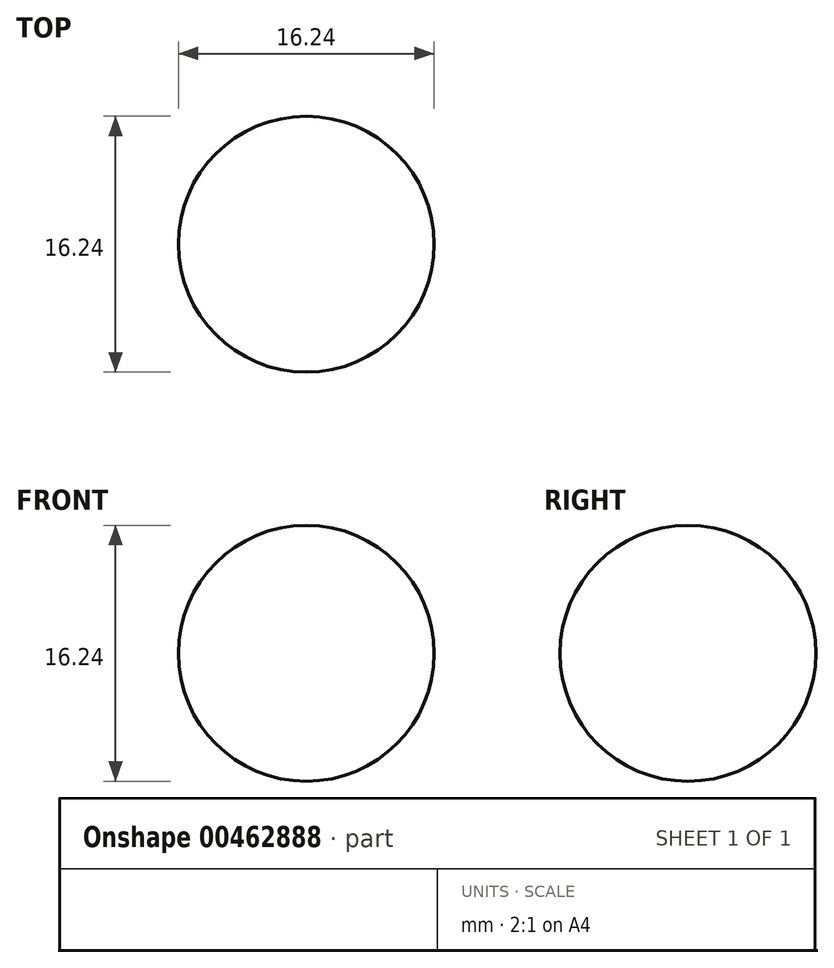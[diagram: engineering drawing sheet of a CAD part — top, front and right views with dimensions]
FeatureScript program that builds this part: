
annotation { "Feature Type Name" : "Feature", "Feature Type Description" : "" }
export const myFeature = defineFeature(function(context is Context, id is Id, definition is map)
    precondition{}
    {
        {
            var Q0;
            Q0=qCreatedBy(makeId("Top.planeOp"),FACE);
            var sketch = newSketch(context, id + "F0", { "sketchPlane" : qUnion([Q0])});
            skCircle(sketch, "E0", {"center": v(0, 0) * mm, "radius": 8.12 * mm});
            skLineSegment(sketch, "E1", {"start": v(-8.12, 0) * mm, "end": v(8.12, 0) * mm});
            skSolve(sketch);
        }
        {
            var Q0;
            {var subQ0=sQuery(id+"F0.wireOp",EDGE,"E1");Q0=makeQuery(id+"F0.imprint","IMPRINT",FACE,{"disambiguationData":[TD([[makeQuery(id+"F0.imprint","IMPRINT",EDGE,{"derivedFrom":subQ0}),1.0]])]});}
            var Q1;
            Q1=sQuery(id+"F0.wireOp",EDGE,"E1");
            revolve(context, id + "F1", {"entities" : qUnion([Q0]), "axis" : qUnion([Q1]), "revolveType" : RevolveType.FULL});
        }
    });
